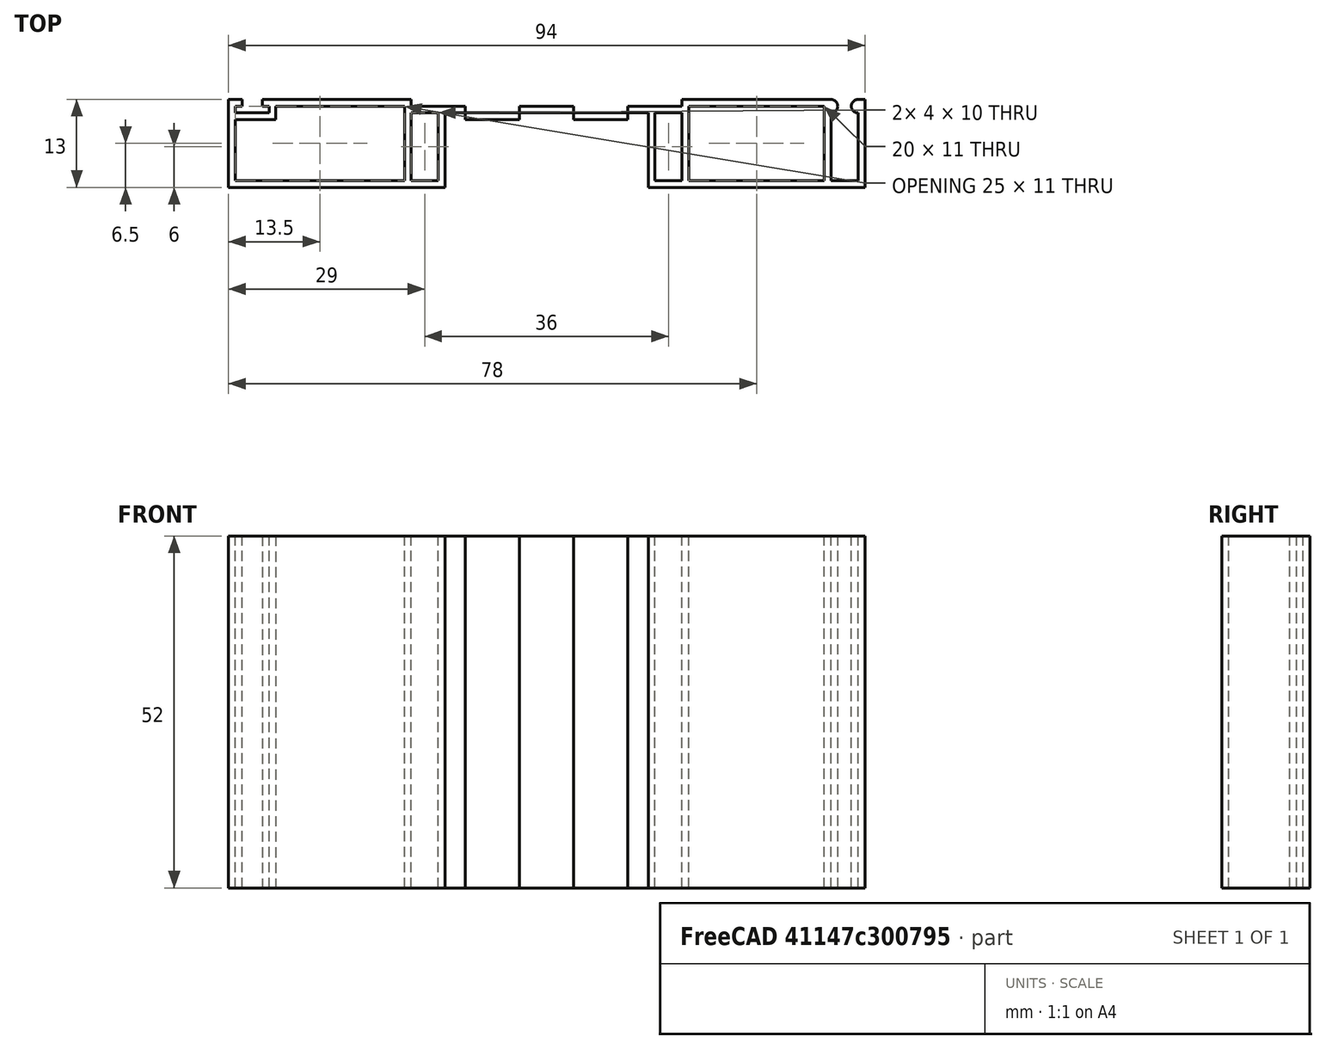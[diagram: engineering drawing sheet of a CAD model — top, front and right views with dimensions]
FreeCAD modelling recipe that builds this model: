
FCSTD DOCUMENT  (FreeCAD 0.16R6700 (Git))
Label: Perfil Aluminio
License: All rights reserved
LicenseURL: http://en.wikipedia.org/wiki/All_rights_reserved
objects: Part::Box×19, Part::Cut×9, Part::MultiFuse×7, Part::Thickness×3, Part::Cylinder×2
note: 40 computed .brp shape members not serialized (recipe doc carries the construction recipe); baked Part::Feature solids carry a one-line shape summary decoded from their .brp

FEATURE [Part::Box] Box  label="Cubo"
  Height = 53
  Length = 30
  Width = 11
FEATURE [Part::Thickness] Thickness
  Faces = -> Box [Face6]
  Intersection = false
  Join = 2
  Mode = 0
  SelfIntersection = false
  Value = 1
FEATURE [Part::Box] Box001  label="Cubo001"
  Height = 53
  Length = 30
  Width = 11
FEATURE [Part::Thickness] Thickness001
  Faces = -> Box001 [Face6]
  Intersection = false
  Join = 2
  Mode = 0
  Placement = pos=(62,0,0) rot=(0,0,1;0rad)
  SelfIntersection = false
  Value = 1
FEATURE [Part::Box] Box002  label="Cubo002"
  Height = 53
  Length = 30
  Width = 11
FEATURE [Part::Thickness] Thickness002
  Faces = -> Box002 [Face6]
  Intersection = false
  Join = 2
  Mode = 0
  Placement = pos=(31,0,0) rot=(0,0,1;0rad)
  SelfIntersection = false
  Value = 1
FEATURE [Part::MultiFuse] Fusion
  Shapes = -> [Thickness001,Thickness002,Thickness]
FEATURE [Part::Box] Box003  label="Cubo003"
  Height = 10
  Length = 100
  Placement = pos=(-4,-5,-9) rot=(0,0,1;0rad)
  Width = 19
FEATURE [Part::Box] Box004  label="Cubo004"
  Height = 53
  Length = 1
  Placement = pos=(66,0,0) rot=(0,0,1;0rad)
  Width = 11
FEATURE [Part::Box] Box005  label="Cubo005"
  Height = 53
  Length = 1
  Placement = pos=(87,0,0) rot=(0,0,1;0rad)
  Width = 11
FEATURE [Part::Box] Box006  label="Cubo006"
  Height = 53
  Length = 1
  Placement = pos=(25,0,0) rot=(0,0,1;0rad)
  Width = 11
FEATURE [Part::Box] Box007  label="Cubo007"
  Height = 53
  Length = 7
  Placement = pos=(-1,9,0) rot=(0,0,1;0rad)
  Width = 3
FEATURE [Part::MultiFuse] Fusion001
  Shapes = -> [Fusion,Box004,Box005,Box006,Box007]
FEATURE [Part::Box] Box008  label="Cubo008"
  Height = 53
  Length = 30
  Placement = pos=(31,-5,0) rot=(0,0,1;0rad)
  Width = 6
FEATURE [Part::Cut] Cut
  Base = -> Fusion001
  Tool = -> Box008
FEATURE [Part::Box] Box009  label="Cubo009"
  Height = 53
  Length = 4
  Placement = pos=(88,10,0) rot=(0,0,1;0rad)
  Width = 3
FEATURE [Part::Cut] Cut001
  Base = -> Cut
  Tool = -> Box009
FEATURE [Part::Box] Box010  label="Cubo010"
  Height = 10
  Length = 5
  Placement = pos=(0,10,0) rot=(0,0,1;0rad)
  Width = 1
FEATURE [Part::Cut] Cut002
  Base = -> Cut001
  Tool = -> Box010
FEATURE [Part::Box] Box011  label="Cubo011"
  Height = 53
  Length = 3
  Placement = pos=(1,11,0) rot=(0,0,1;0rad)
  Width = 4
FEATURE [Part::Cut] Cut003
  Base = -> Cut002
  Tool = -> Box011
FEATURE [Part::Cut] Cut004
  Base = -> Cut003
  Tool = -> Box003
FEATURE [Part::Box] Box012  label="Cubo012"
  Height = 68
  Length = 5
  Placement = pos=(0,10,-13) rot=(0,0,1;0rad)
  Width = 1
FEATURE [Part::Cut] Cut005
  Base = -> Cut004
  Tool = -> Box012
FEATURE [Part::Cylinder] Cylinder  label="Cilindro"
  Angle = 360
  Height = 52
  Placement = pos=(88,11,1) rot=(0,0,1;0rad)
  Radius = 1
FEATURE [Part::MultiFuse] Fusion002
  Shapes = -> [Cut005,Cylinder]
FEATURE [Part::Cylinder] Cylinder001  label="Cilindro001"
  Angle = 360
  Height = 52
  Placement = pos=(92,11,1) rot=(0,0,1;0rad)
  Radius = 1
FEATURE [Part::MultiFuse] Fusion003
  Shapes = -> [Fusion002,Cylinder001]
FEATURE [Part::Box] Box013  label="Cubo013"
  Height = 52
  Length = 40
  Placement = pos=(26,10,1) rot=(0,0,1;0rad)
  Width = 1
FEATURE [Part::Box] Box014  label="Cubo014"
  Height = 52
  Length = 40
  Placement = pos=(26,11,1) rot=(0,0,1;0rad)
  Width = 1
FEATURE [Part::MultiFuse] Fusion004
  Shapes = -> [Fusion003,Box013]
FEATURE [Part::Cut] Cut006
  Base = -> Fusion004
  Placement = pos=(131,27,1) rot=(0,0,1;0rad)
  Tool = -> Box014
FEATURE [Part::Box] Box015  label="Cubo015"
  Height = 52
  Length = 8
  Placement = pos=(181,36,2) rot=(0,0,1;0rad)
  Width = 1
FEATURE [Part::Box] Box016  label="Cubo016"
  Height = 52
  Length = 8
  Placement = pos=(165,37,2) rot=(0,0,1;0rad)
  Width = 1
FEATURE [Part::MultiFuse] Fusion005
  Shapes = -> [Cut006,Box015]
FEATURE [Part::Box] Box017  label="Cubo017"
  Height = 52
  Length = 8
  Placement = pos=(165,36,2) rot=(0,0,1;0rad)
  Width = 1
FEATURE [Part::Box] Box018  label="Cubo018"
  Height = 52
  Length = 8
  Placement = pos=(181,37,2) rot=(0,0,1;0rad)
  Width = 1
FEATURE [Part::MultiFuse] Fusion006
  Shapes = -> [Fusion005,Box017]
FEATURE [Part::Cut] Cut007
  Base = -> Fusion006
  Tool = -> Box016
FEATURE [Part::Cut] Cut008
  Base = -> Cut007
  Tool = -> Box018
